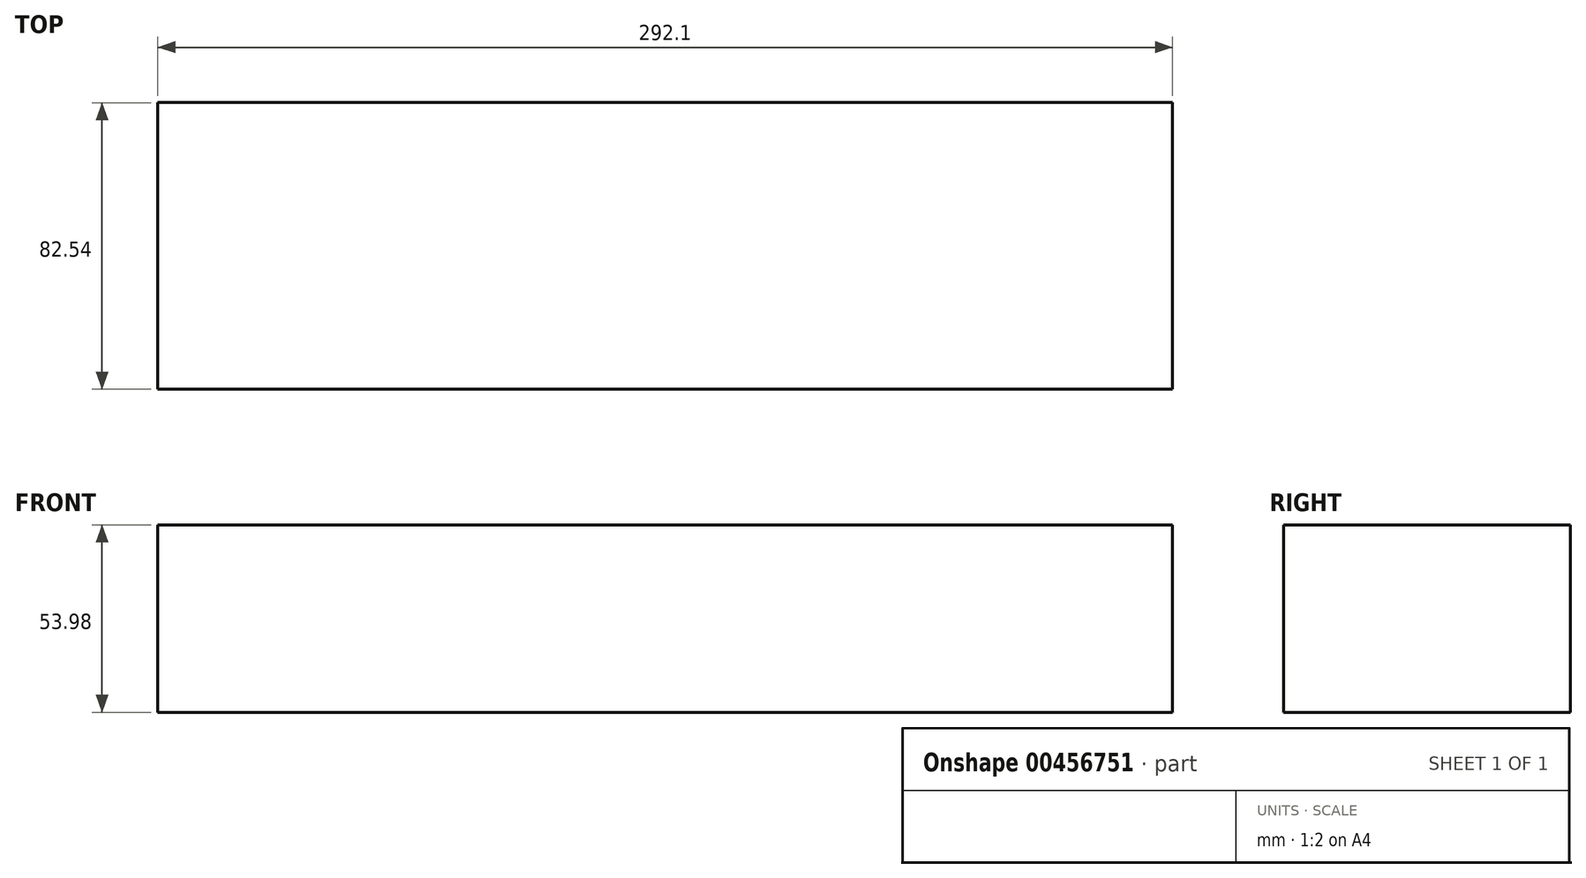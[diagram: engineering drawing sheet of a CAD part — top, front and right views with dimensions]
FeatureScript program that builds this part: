
annotation { "Feature Type Name" : "Feature", "Feature Type Description" : "" }
export const myFeature = defineFeature(function(context is Context, id is Id, definition is map)
    precondition{}
    {
        {
            var Q0;
            Q0=qCreatedBy(makeId("Top.planeOp"),FACE);
            var sketch = newSketch(context, id + "F0", { "sketchPlane" : qUnion([Q0])});
            skLineSegment(sketch, "E0.bottom", {"start": v(-146.05, 41.27) * mm, "end": v(146.05, 41.27) * mm});
            skLineSegment(sketch, "E0.top", {"start": v(-146.05, -41.27) * mm, "end": v(146.05, -41.27) * mm});
            skLineSegment(sketch, "E0.left", {"start": v(-146.05, 41.27) * mm, "end": v(-146.05, -41.27) * mm});
            skLineSegment(sketch, "E0.right", {"start": v(146.05, 41.27) * mm, "end": v(146.05, -41.27) * mm});
            skPoint(sketch, "E0.middle", {"position": v(0, 0) * mm});
            skSolve(sketch);
        }
        {
            var Q0;
            Q0=makeQuery(id+"F0.imprint","IMPRINT",FACE,{"disambiguationData":[TD([[makeQuery(id+"F0.imprint","IMPRINT",EDGE,{"derivedFrom":sQuery(id+"F0.wireOp",EDGE,"E0.bottom")}),-1.0]])]});
            extrude(context, id + "F1", {"entities" : qUnion([Q0]), "depth" : 53.97 * mm});
        }
    });
